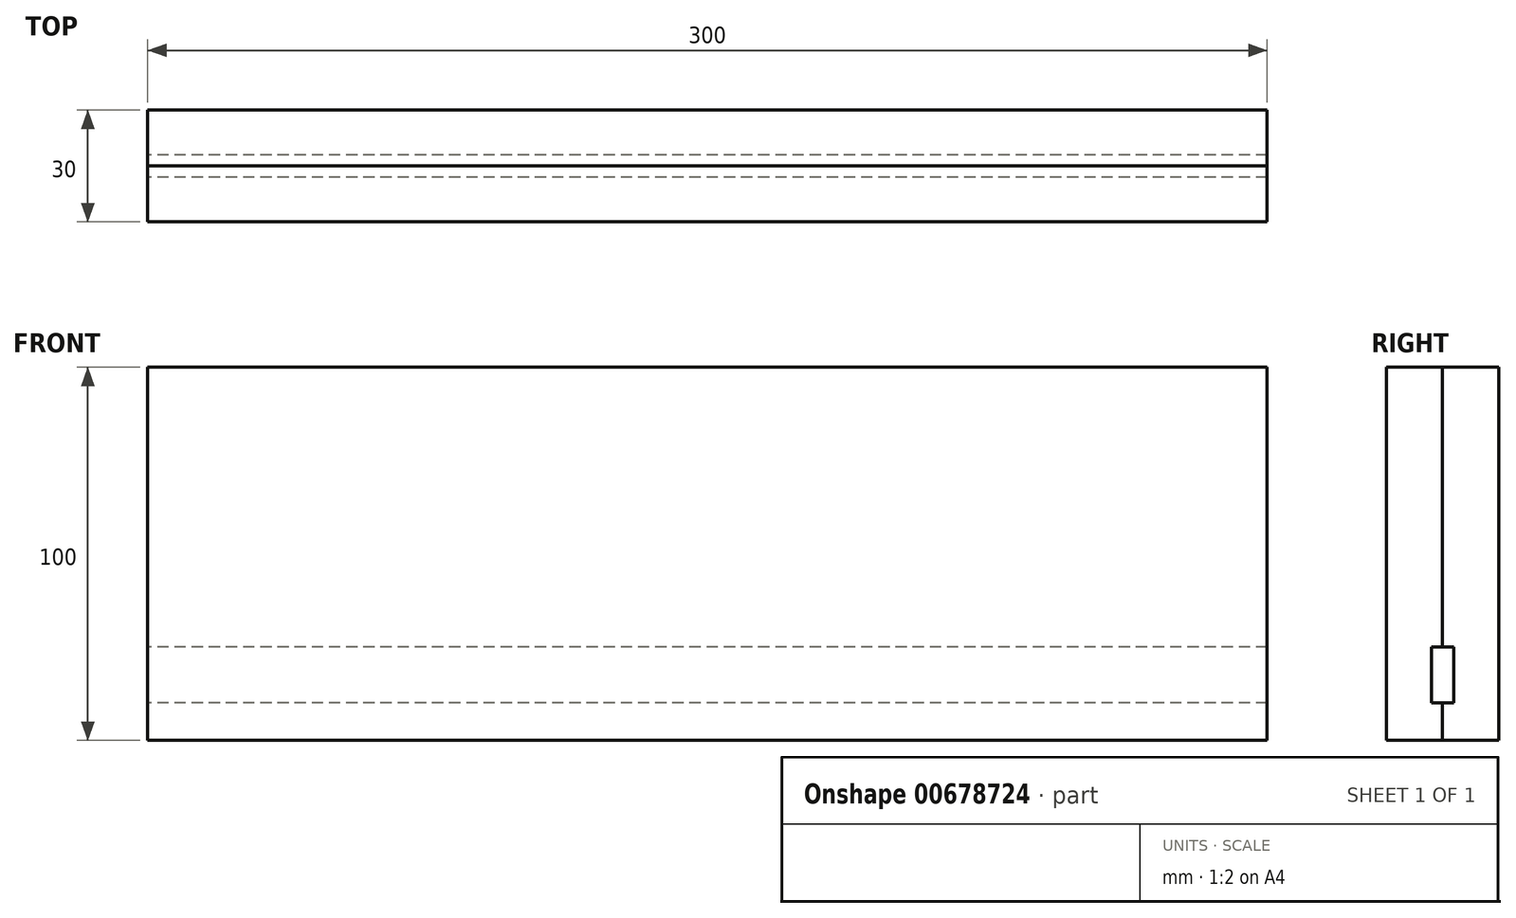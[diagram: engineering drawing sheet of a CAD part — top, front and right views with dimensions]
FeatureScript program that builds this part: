
annotation { "Feature Type Name" : "Feature", "Feature Type Description" : "" }
export const myFeature = defineFeature(function(context is Context, id is Id, definition is map)
    precondition{}
    {
        {
            var Q0;
            Q0=qCreatedBy(makeId("Right.planeOp"),FACE);
            var sketch = newSketch(context, id + "F0", { "sketchPlane" : qUnion([Q0])});
            skLineSegment(sketch, "E0", {"start": v(0, 0) * mm, "end": v(-15, 0) * mm});
            skLineSegment(sketch, "E1", {"start": v(-15, 0) * mm, "end": v(-15, 100) * mm});
            skLineSegment(sketch, "E2", {"start": v(-15, 100) * mm, "end": v(0, 100) * mm});
            skLineSegment(sketch, "E3", {"start": v(0, 100) * mm, "end": v(0, 25) * mm});
            skLineSegment(sketch, "E4", {"start": v(0, 25) * mm, "end": v(-3, 25) * mm});
            skLineSegment(sketch, "E5", {"start": v(-3, 25) * mm, "end": v(-3, 10) * mm});
            skLineSegment(sketch, "E6", {"start": v(-3, 10) * mm, "end": v(0, 10) * mm});
            skLineSegment(sketch, "E7", {"start": v(0, 10) * mm, "end": v(0, 0) * mm});
            skSolve(sketch);
        }
        {
            var Q0;
            Q0 = qSketchRegion(id + "F0", true);
            extrude(context, id + "F1", {"entities" : qUnion([Q0]), "endBound" : BoundingType.SYMMETRIC, "depth" : 300 * mm, "offsetDistance" : 25 * mm});
        }
        {
            var Q0;
            Q0=makeQuery(id+"F1.opExtrude","SWEPT_BODY",BODY,{"disambiguationData":[OSD([sQuery(id+"F0.wireOp",EDGE,"E0"),sQuery(id+"F0.wireOp",EDGE,"E1"),sQuery(id+"F0.wireOp",EDGE,"E2"),sQuery(id+"F0.wireOp",EDGE,"E3"),sQuery(id+"F0.wireOp",EDGE,"E4"),sQuery(id+"F0.wireOp",EDGE,"E5"),sQuery(id+"F0.wireOp",EDGE,"E6"),sQuery(id+"F0.wireOp",EDGE,"E7")])]});
            var Q1;
            Q1=qCreatedBy(makeId("Front.planeOp"),FACE);
            mirror(context, id + "F2", {"entities" : qUnion([Q0]), "mirrorPlane" : qUnion([Q1])});
        }
    });
